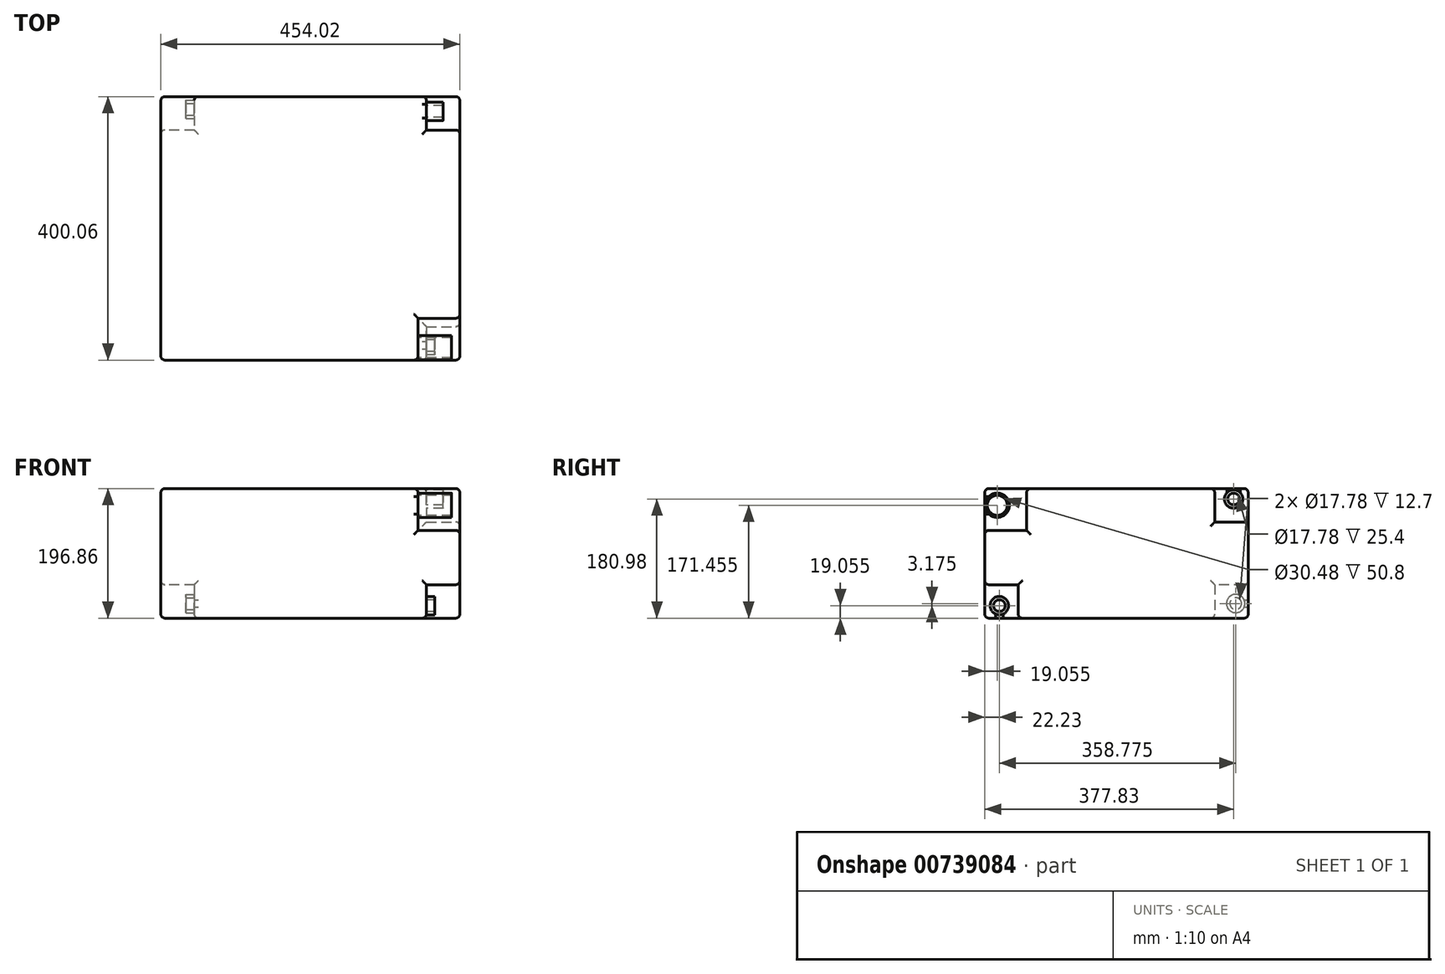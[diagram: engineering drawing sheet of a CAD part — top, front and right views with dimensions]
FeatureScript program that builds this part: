
annotation { "Feature Type Name" : "Feature", "Feature Type Description" : "" }
export const myFeature = defineFeature(function(context is Context, id is Id, definition is map)
    precondition{}
    {
        {
            var Q0;
            Q0=qCreatedBy(makeId("Top.planeOp"),FACE);
            var sketch = newSketch(context, id + "F0", { "sketchPlane" : qUnion([Q0])});
            skLineSegment(sketch, "E0.bottom", {"start": v(-227.01, 200.03) * mm, "end": v(227.01, 200.03) * mm});
            skLineSegment(sketch, "E0.top", {"start": v(-227.01, -200.02) * mm, "end": v(227.01, -200.02) * mm});
            skLineSegment(sketch, "E0.left", {"start": v(-227.01, 200.03) * mm, "end": v(-227.01, -200.02) * mm});
            skLineSegment(sketch, "E0.right", {"start": v(227.01, 200.03) * mm, "end": v(227.01, -200.02) * mm});
            skPoint(sketch, "E0.middle", {"position": v(0, 0) * mm});
            skSolve(sketch);
        }
        {
            var Q0;
            Q0 = qSketchRegion(id + "F0", true);
            extrude(context, id + "F1", {"entities" : qUnion([Q0]), "endBound" : BoundingType.SYMMETRIC, "depth" : 196.85 * mm, "offsetDistance" : 25.4 * mm});
        }
        {
            var Q0;
            Q0=makeQuery(id+"F1.opExtrude","SWEPT_FACE",FACE,{"disambiguationData":[OSD([sQuery(id+"F0.wireOp",EDGE,"E0.right")])]});
            var sketch = newSketch(context, id + "F2", { "sketchPlane" : qUnion([Q0])});
            skLineSegment(sketch, "E1", {"start": v(-200.02, -47.63) * mm, "end": v(-149.22, -47.63) * mm});
            skLineSegment(sketch, "E2", {"start": v(-149.22, -47.63) * mm, "end": v(-149.22, -98.43) * mm});
            skLineSegment(sketch, "E3", {"start": v(-200.02, 34.93) * mm, "end": v(-136.52, 34.93) * mm});
            skLineSegment(sketch, "E4", {"start": v(-136.52, 34.93) * mm, "end": v(-136.52, 98.43) * mm});
            skLineSegment(sketch, "E5", {"start": v(149.23, 98.43) * mm, "end": v(149.23, 47.63) * mm});
            skLineSegment(sketch, "E6", {"start": v(149.23, 47.63) * mm, "end": v(200.03, 47.63) * mm});
            skSolve(sketch);
        }
        {
            var Q0;
            {var subQ0=sQuery(id+"F2.wireOp",EDGE,"E1");Q0=makeQuery(id+"F2.imprint","IMPRINT",FACE,{"disambiguationData":[TD([[makeQuery(id+"F2.imprint","IMPRINT",EDGE,{"derivedFrom":subQ0}),-1.0]])]});}
            var Q1;
            {var subQ0=sQuery(id+"F2.wireOp",EDGE,"E5");Q1=makeQuery(id+"F2.imprint","IMPRINT",FACE,{"disambiguationData":[TD([[makeQuery(id+"F2.imprint","IMPRINT",EDGE,{"derivedFrom":subQ0}),1.0]])]});}
            extrude(context, id + "F3", {"entities" : qUnion([Q0, Q1]), "operationType" : NewBodyOperationType.REMOVE, "oppositeDirection" : true, "depth" : 50.8 * mm, "offsetDistance" : 25.4 * mm});
        }
        {
            var Q0;
            {var subQ0=sQuery(id+"F2.wireOp",EDGE,"E3");Q0=makeQuery(id+"F2.imprint","IMPRINT",FACE,{"disambiguationData":[TD([[makeQuery(id+"F2.imprint","IMPRINT",EDGE,{"derivedFrom":subQ0}),1.0]])]});}
            extrude(context, id + "F4", {"entities" : qUnion([Q0]), "operationType" : NewBodyOperationType.REMOVE, "oppositeDirection" : true, "depth" : 63.5 * mm, "offsetDistance" : 25.4 * mm});
        }
        {
            var Q0;
            Q0=makeQuery(id+"F1.opExtrude","SWEPT_FACE",FACE,{"disambiguationData":[OSD([sQuery(id+"F0.wireOp",EDGE,"E0.left")])]});
            var sketch = newSketch(context, id + "F5", { "sketchPlane" : qUnion([Q0])});
            skLineSegment(sketch, "E7", {"start": v(-200.03, -47.63) * mm, "end": v(-149.22, -47.63) * mm});
            skLineSegment(sketch, "E8", {"start": v(-149.22, -47.63) * mm, "end": v(-149.22, -98.43) * mm});
            skSolve(sketch);
        }
        {
            var Q0;
            {var subQ0=sQuery(id+"F5.wireOp",EDGE,"E7");Q0=makeQuery(id+"F5.imprint","IMPRINT",FACE,{"disambiguationData":[TD([[makeQuery(id+"F5.imprint","IMPRINT",EDGE,{"derivedFrom":subQ0}),-1.0]])]});}
            extrude(context, id + "F6", {"entities" : qUnion([Q0]), "operationType" : NewBodyOperationType.REMOVE, "oppositeDirection" : true, "depth" : 50.8 * mm, "offsetDistance" : 25.4 * mm});
        }
        {
            var Q0;
            Q0=makeQuery(id+"F3.boolean.opBoolean","COPY",FACE,{"derivedFrom":makeQuery(id+"F3.opExtrude","CAP_FACE",FACE,{"disambiguationData":[OSD([sQuery(id+"F0.wireOp",EDGE,"E0.bottom"),sQuery(id+"F0.wireOp",EDGE,"E0.right"),sQuery(id+"F2.wireOp",EDGE,"E5"),sQuery(id+"F2.wireOp",EDGE,"E6")])],"isStart":false})});
            var sketch = newSketch(context, id + "F7", { "sketchPlane" : qUnion([Q0])});
            skCircle(sketch, "E9", {"center": v(177.8, 82.55) * mm, "radius": 13.97 * mm});
            skCircle(sketch, "E10", {"center": v(177.8, 82.55) * mm, "radius": 8.9 * mm});
            skCircle(sketch, "E11", {"center": v(-177.8, -79.38) * mm, "radius": 8.9 * mm});
            skCircle(sketch, "E12", {"center": v(-177.8, -79.38) * mm, "radius": 13.97 * mm});
            skSolve(sketch);
        }
        {
            var Q0;
            Q0=makeQuery(id+"F7.imprint","IMPRINT",FACE,{"disambiguationData":[TD([[makeQuery(id+"F7.imprint","IMPRINT",EDGE,{"derivedFrom":sQuery(id+"F7.wireOp",EDGE,"E9")}),1.0]])]});
            extrude(context, id + "F8", {"entities" : qUnion([Q0]), "operationType" : NewBodyOperationType.ADD, "depth" : 25.4 * mm, "offsetDistance" : 25.4 * mm});
        }
        {
            var Q0;
            Q0=makeQuery(id+"F6.boolean.opBoolean","COPY",FACE,{"derivedFrom":makeQuery(id+"F6.opExtrude","CAP_FACE",FACE,{"disambiguationData":[OSD([sQuery(id+"F0.wireOp",EDGE,"E0.bottom"),sQuery(id+"F0.wireOp",EDGE,"E0.left"),sQuery(id+"F5.wireOp",EDGE,"E7"),sQuery(id+"F5.wireOp",EDGE,"E8")])],"isStart":false})});
            var sketch = newSketch(context, id + "F9", { "sketchPlane" : qUnion([Q0])});
            skCircle(sketch, "E13", {"center": v(-180.98, -76.2) * mm, "radius": 13.97 * mm});
            skCircle(sketch, "E14", {"center": v(-180.98, -76.2) * mm, "radius": 8.9 * mm});
            skSolve(sketch);
        }
        {
            var Q0;
            Q0 = qSketchRegion(id + "F9", true);
            extrude(context, id + "F10", {"entities" : qUnion([Q0]), "operationType" : NewBodyOperationType.ADD, "depth" : 12.7 * mm, "offsetDistance" : 25.4 * mm});
        }
        {
            var Q0;
            Q0 = qSketchRegion(id + "F7", true);
            extrude(context, id + "F11", {"entities" : qUnion([Q0]), "operationType" : NewBodyOperationType.ADD, "depth" : 12.7 * mm, "offsetDistance" : 25.4 * mm});
        }
        {
            var Q0;
            Q0=makeQuery(id+"F4.boolean.opBoolean","COPY",FACE,{"derivedFrom":makeQuery(id+"F4.opExtrude","CAP_FACE",FACE,{"disambiguationData":[OSD([sQuery(id+"F0.wireOp",EDGE,"E0.top"),sQuery(id+"F0.wireOp",EDGE,"E0.right"),sQuery(id+"F2.wireOp",EDGE,"E3"),sQuery(id+"F2.wireOp",EDGE,"E4")])],"isStart":false})});
            var sketch = newSketch(context, id + "F12", { "sketchPlane" : qUnion([Q0])});
            skCircle(sketch, "E15", {"center": v(-180.97, 73.03) * mm, "radius": 18.41 * mm});
            skCircle(sketch, "E16", {"center": v(-180.97, 73.03) * mm, "radius": 15.24 * mm});
            skSolve(sketch);
        }
        {
            var Q0;
            Q0 = qSketchRegion(id + "F12", true);
            extrude(context, id + "F13", {"entities" : qUnion([Q0]), "operationType" : NewBodyOperationType.ADD, "depth" : 50.8 * mm, "offsetDistance" : 25.4 * mm});
        }
        {
            var Q0;
            Q0=makeQuery(id+"F1.opExtrude","SWEPT_FACE",FACE,{"disambiguationData":[OSD([sQuery(id+"F0.wireOp",EDGE,"E0.right")])]});
            var Q1;
            Q1=makeQuery(id+"F1.opExtrude","SWEPT_FACE",FACE,{"disambiguationData":[OSD([sQuery(id+"F0.wireOp",EDGE,"E0.bottom")])]});
            var Q2;
            Q2=makeQuery(id+"F1.opExtrude","CAP_FACE",FACE,{"disambiguationData":[OSD([sQuery(id+"F0.wireOp",EDGE,"E0.bottom"),sQuery(id+"F0.wireOp",EDGE,"E0.top"),sQuery(id+"F0.wireOp",EDGE,"E0.left"),sQuery(id+"F0.wireOp",EDGE,"E0.right")])],"isStart":true});
            var Q3;
            Q3=makeQuery(id+"F1.opExtrude","CAP_FACE",FACE,{"disambiguationData":[OSD([sQuery(id+"F0.wireOp",EDGE,"E0.bottom"),sQuery(id+"F0.wireOp",EDGE,"E0.top"),sQuery(id+"F0.wireOp",EDGE,"E0.left"),sQuery(id+"F0.wireOp",EDGE,"E0.right")])],"isStart":false});
            var Q4;
            Q4=makeQuery(id+"F1.opExtrude","SWEPT_FACE",FACE,{"disambiguationData":[OSD([sQuery(id+"F0.wireOp",EDGE,"E0.left")])]});
            var Q5;
            Q5=makeQuery(id+"F1.opExtrude","SWEPT_FACE",FACE,{"disambiguationData":[OSD([sQuery(id+"F0.wireOp",EDGE,"E0.top")])]});
            fillet(context, id + "F14", {"entities" : qUnion([Q0, Q1, Q2, Q3, Q4, Q5]), "radius" : 6.35 * mm, "tangentPropagation" : true, "allowEdgeOverflow" : false});
        }
    });
